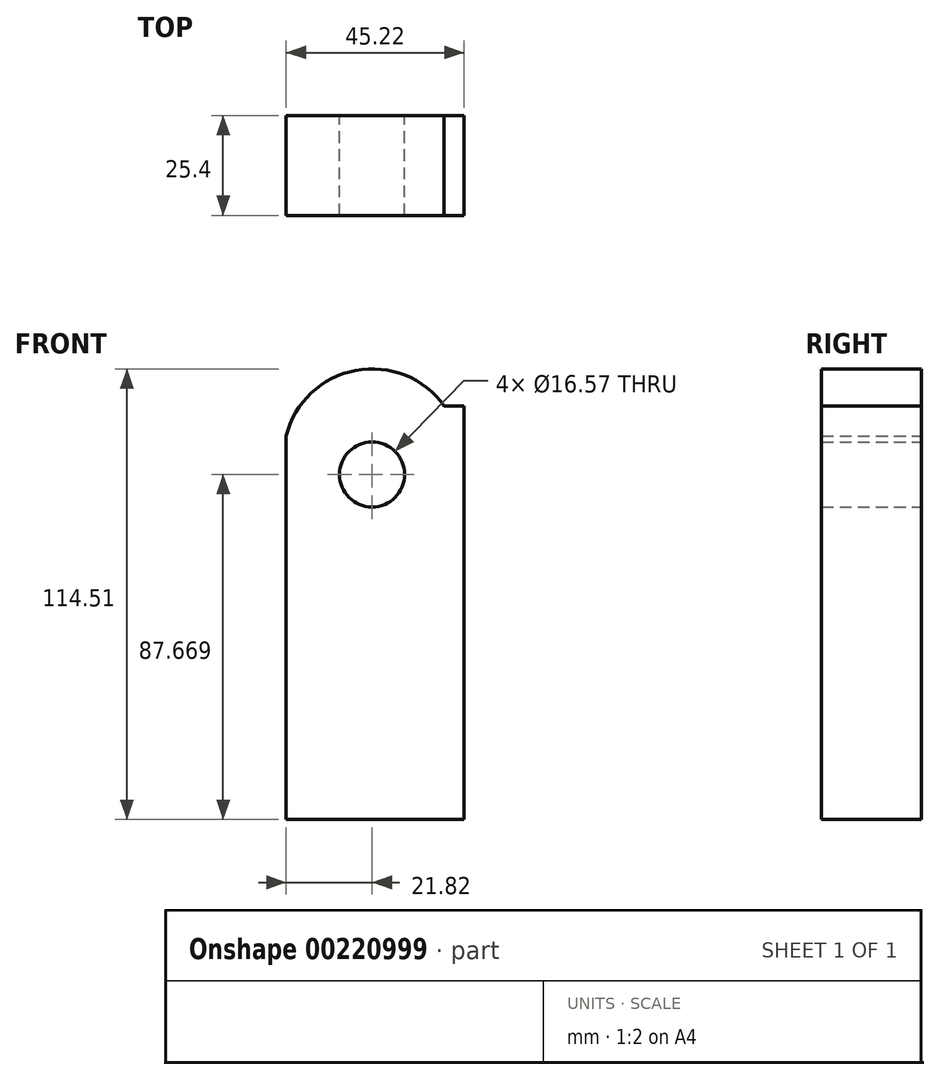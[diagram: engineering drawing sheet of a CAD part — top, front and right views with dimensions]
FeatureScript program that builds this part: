
annotation { "Feature Type Name" : "Feature", "Feature Type Description" : "" }
export const myFeature = defineFeature(function(context is Context, id is Id, definition is map)
    precondition{}
    {
        {
            var Q0;
            Q0=qCreatedBy(makeId("Front.planeOp"),FACE);
            var sketch = newSketch(context, id + "F0", { "sketchPlane" : qUnion([Q0])});
            skLineSegment(sketch, "E0", {"start": v(-21.82, 44.24) * mm, "end": v(-21.82, -60.29) * mm});
            skLineSegment(sketch, "E1", {"start": v(-21.82, -60.29) * mm, "end": v(23.4, -60.29) * mm});
            skLineSegment(sketch, "E2", {"start": v(23.4, -60.29) * mm, "end": v(23.4, 44.83) * mm});
            skLineSegment(sketch, "E3", {"start": v(-21.82, 44.24) * mm, "end": v(23.4, 44.83) * mm});
            skCircle(sketch, "E4", {"center": v(0, 31.74) * mm, "radius": 22.48 * mm});
            skCircle(sketch, "E5", {"center": v(0, 27.38) * mm, "radius": 8.28 * mm});
            skSolve(sketch);
        }
        {
            var Q0;
            Q0=makeQuery(id+"F0.imprint","IMPRINT",FACE,{"disambiguationData":[TD([[makeQuery(id+"F0.imprint","IMPRINT",EDGE,{"derivedFrom":sQuery(id+"F0.wireOp",EDGE,"E5")}),-1.0]])]});
            var Q1;
            {var subQ0=sQuery(id+"F0.wireOp",EDGE,"E4");var subQ1=sQuery(id+"F0.wireOp",EDGE,"E3");var subQ2=makeQuery(id+"F0.imprint","INTERSECT",VERTEX,{"disambiguationData":[OD(0.0)],"derivedFrom":[subQ1,subQ0]});Q1=makeQuery(id+"F0.imprint","IMPRINT",FACE,{"disambiguationData":[TD([[makeQuery(id+"F0.imprint","IMPRINT",EDGE,{"disambiguationData":[TD([[subQ2,-1.0]])],"derivedFrom":subQ1}),1.0]])]});}
            var Q2;
            {var subQ4=sQuery(id+"F0.wireOp",EDGE,"E1");Q2=makeQuery(id+"F0.imprint","IMPRINT",FACE,{"disambiguationData":[TD([[makeQuery(id+"F0.imprint","IMPRINT",EDGE,{"derivedFrom":subQ4}),1.0]])]});}
            extrude(context, id + "F1", {"entities" : qUnion([Q0, Q1, Q2]), "depth" : 25.4 * mm});
        }
    });
